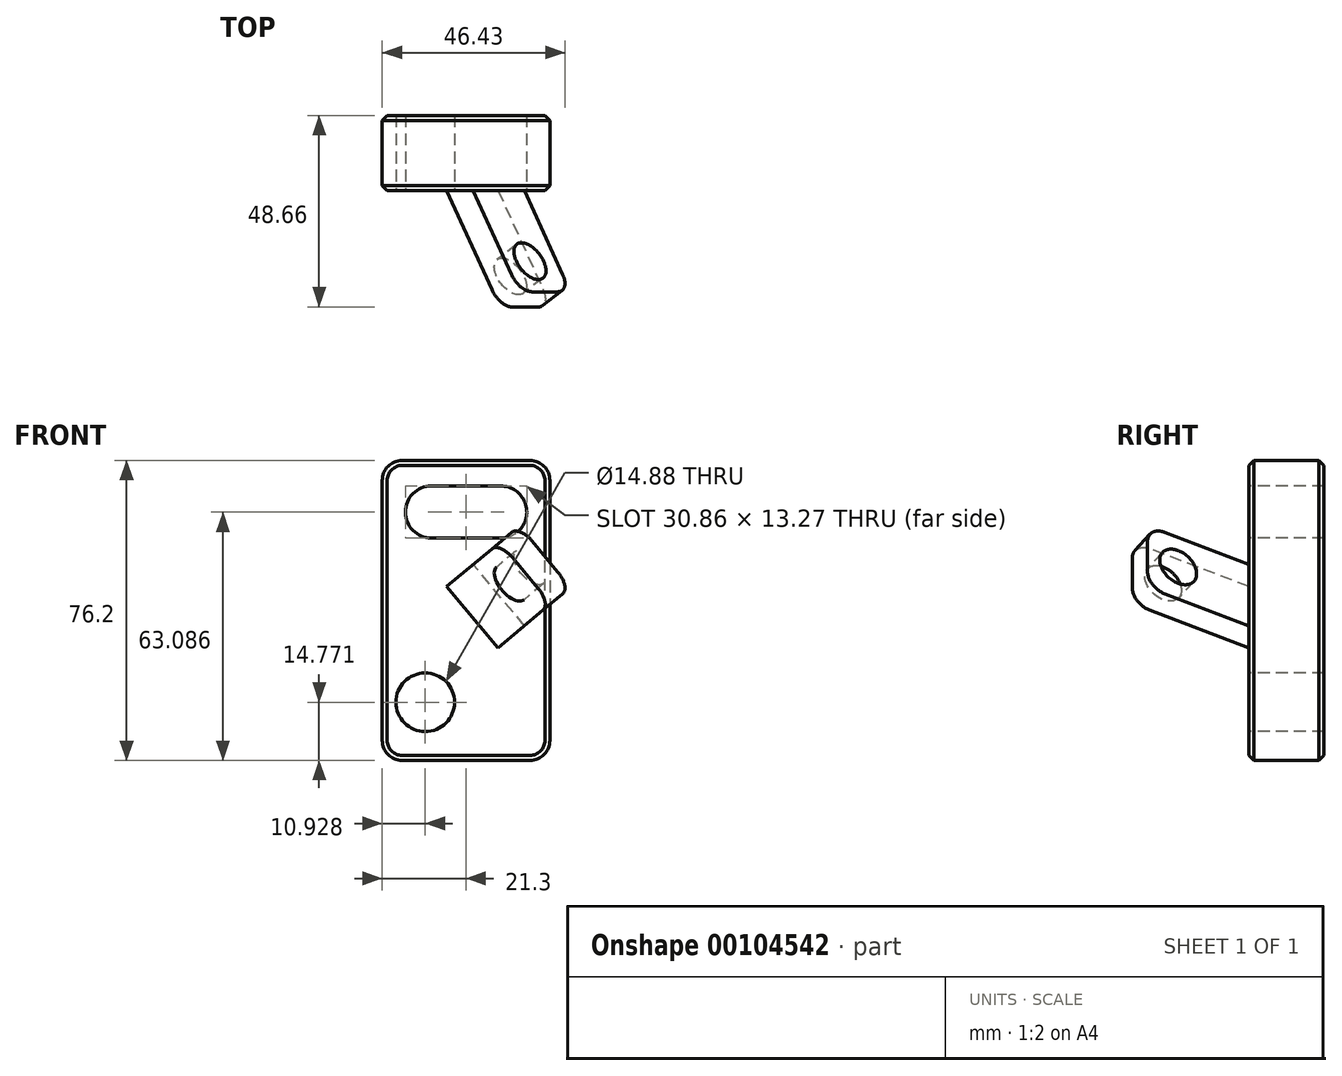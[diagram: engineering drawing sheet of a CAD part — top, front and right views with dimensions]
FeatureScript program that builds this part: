
annotation { "Feature Type Name" : "Feature", "Feature Type Description" : "" }
export const myFeature = defineFeature(function(context is Context, id is Id, definition is map)
    precondition{}
    {
        {
            var Q0;
            Q0=qCreatedBy(makeId("Front.planeOp"),FACE);
            var sketch = newSketch(context, id + "F0", { "sketchPlane" : qUnion([Q0])});
            skLineSegment(sketch, "E0.bottom", {"start": v(21.3, -38.1) * mm, "end": v(-21.3, -38.1) * mm});
            skLineSegment(sketch, "E0.top", {"start": v(21.3, 38.1) * mm, "end": v(-21.3, 38.1) * mm});
            skLineSegment(sketch, "E0.left", {"start": v(21.3, -38.1) * mm, "end": v(21.3, 38.1) * mm});
            skLineSegment(sketch, "E0.right", {"start": v(-21.3, -38.1) * mm, "end": v(-21.3, 38.1) * mm});
            skPoint(sketch, "E0.middle", {"position": v(0, 0) * mm});
            skSolve(sketch);
        }
        {
            var Q0;
            Q0 = qSketchRegion(id + "F0", true);
            extrude(context, id + "F1", {"entities" : qUnion([Q0]), "depth" : 19.05 * mm});
        }
        {
            var Q0;
            Q0=makeQuery(id+"F1.opExtrude","SWEPT_EDGE",EDGE,{"disambiguationData":[OSD([sQuery(id+"F0.wireOp",EDGE,"E0.top"),sQuery(id+"F0.wireOp",EDGE,"E0.right")])]});
            var Q1;
            Q1=makeQuery(id+"F1.opExtrude","SWEPT_EDGE",EDGE,{"disambiguationData":[OSD([sQuery(id+"F0.wireOp",EDGE,"E0.top"),sQuery(id+"F0.wireOp",EDGE,"E0.left")])]});
            var Q2;
            Q2=makeQuery(id+"F1.opExtrude","SWEPT_EDGE",EDGE,{"disambiguationData":[OSD([sQuery(id+"F0.wireOp",EDGE,"E0.bottom"),sQuery(id+"F0.wireOp",EDGE,"E0.left")])]});
            var Q3;
            Q3=makeQuery(id+"F1.opExtrude","SWEPT_EDGE",EDGE,{"disambiguationData":[OSD([sQuery(id+"F0.wireOp",EDGE,"E0.bottom"),sQuery(id+"F0.wireOp",EDGE,"E0.right")])]});
            fillet(context, id + "F2", {"entities" : qUnion([Q0, Q1, Q2, Q3]), "radius" : 5.08 * mm, "tangentPropagation" : true, "allowEdgeOverflow" : false});
        }
        {
            var Q0;
            Q0=makeQuery(id+"F1.opExtrude","CAP_FACE",FACE,{"disambiguationData":[OSD([sQuery(id+"F0.wireOp",EDGE,"E0.bottom"),sQuery(id+"F0.wireOp",EDGE,"E0.top"),sQuery(id+"F0.wireOp",EDGE,"E0.left"),sQuery(id+"F0.wireOp",EDGE,"E0.right")])],"isStart":false});
            var sketch = newSketch(context, id + "F3", { "sketchPlane" : qUnion([Q0])});
            skArc(sketch, "E1", {"start": v(-8.8, 31.62) * mm, "mid": v(-15.43, 24.99) * mm, "end": v(-8.8, 18.35) * mm});
            skArc(sketch, "E2.MirrorC", {"start": v(8.8, 31.62) * mm, "mid": v(15.43, 24.99) * mm, "end": v(8.8, 18.35) * mm});
            skLineSegment(sketch, "E3", {"start": v(-8.8, 31.62) * mm, "end": v(8.8, 31.62) * mm});
            skLineSegment(sketch, "E4", {"start": v(-8.8, 18.35) * mm, "end": v(8.8, 18.35) * mm});
            skCircle(sketch, "E5", {"center": v(-10.37, -23.33) * mm, "radius": 7.44 * mm});
            skSolve(sketch);
        }
        {
            var Q0;
            Q0=makeQuery(id+"F3.imprint","IMPRINT",FACE,{"disambiguationData":[TD([[makeQuery(id+"F3.imprint","IMPRINT",EDGE,{"derivedFrom":sQuery(id+"F3.wireOp",EDGE,"E5")}),1.0]])]});
            var Q1;
            Q1=makeQuery(id+"F3.imprint","IMPRINT",FACE,{"disambiguationData":[TD([[makeQuery(id+"F3.imprint","IMPRINT",EDGE,{"derivedFrom":sQuery(id+"F3.wireOp",EDGE,"E1")}),1.0]])]});
            extrude(context, id + "F4", {"entities" : qUnion([Q0, Q1]), "operationType" : NewBodyOperationType.REMOVE, "oppositeDirection" : true, "depth" : 25.4 * mm});
        }
        {
            var Q0;
            Q0=makeQuery(id+"F1.opExtrude","CAP_FACE",FACE,{"disambiguationData":[OSD([sQuery(id+"F0.wireOp",EDGE,"E0.bottom"),sQuery(id+"F0.wireOp",EDGE,"E0.top"),sQuery(id+"F0.wireOp",EDGE,"E0.left"),sQuery(id+"F0.wireOp",EDGE,"E0.right")])],"isStart":false});
            var sketch = newSketch(context, id + "F5", { "sketchPlane" : qUnion([Q0])});
            skLineSegment(sketch, "E6", {"start": v(-8.08, -9.8) * mm, "end": v(16.46, 10.7) * mm, "construction": true});
            skSolve(sketch);
        }
        {
            var Q0;
            Q0=qCreatedBy(makeId("Top.planeOp"),FACE);
            var Q1;
            Q1=sQuery(id+"F5.wireOp",EDGE,"E6");
            cPlane(context, id + "F6", {"entities" : qUnion([Q0, Q1]), "cplaneType" : CPlaneType.LINE_ANGLE, "offset" : 25.4 * mm, "angle" : 0 * degree, "width" : 152.4 * mm, "height" : 152.4 * mm});
        }
        {
            var Q0;
            Q0=qCreatedBy(id+"F6.planeOp",FACE);
            var sketch = newSketch(context, id + "F7", { "sketchPlane" : qUnion([Q0])});
            skLineSegment(sketch, "E7", {"start": v(8.89, 19.05) * mm, "end": v(0.1, 19.05) * mm});
            skLineSegment(sketch, "E8", {"start": v(0.1, 19.05) * mm, "end": v(17.65, 48.66) * mm});
            skLineSegment(sketch, "E9", {"start": v(17.65, 48.66) * mm, "end": v(24.16, 44.8) * mm});
            skLineSegment(sketch, "E10", {"start": v(24.16, 44.8) * mm, "end": v(8.89, 19.05) * mm});
            skSolve(sketch);
        }
        {
            var Q0;
            Q0 = qSketchRegion(id + "F7", true);
            extrude(context, id + "F8", {"entities" : qUnion([Q0]), "operationType" : NewBodyOperationType.ADD, "endBound" : BoundingType.SYMMETRIC, "depth" : 20.32 * mm});
        }
        {
            var Q0;
            Q0=makeQuery(id+"F8.opExtrude","CAP_EDGE",EDGE,{"disambiguationData":[OSD([sQuery(id+"F7.wireOp",EDGE,"E9")])],"isStart":true});
            var Q1;
            Q1=makeQuery(id+"F8.opExtrude","CAP_EDGE",EDGE,{"disambiguationData":[OSD([sQuery(id+"F7.wireOp",EDGE,"E9")])],"isStart":false});
            fillet(context, id + "F9", {"entities" : qUnion([Q0, Q1]), "radius" : 5.08 * mm, "tangentPropagation" : true, "allowEdgeOverflow" : false});
        }
        {
            var Q0;
            Q0=makeQuery(id+"F8.opExtrude","SWEPT_FACE",FACE,{"disambiguationData":[OSD([sQuery(id+"F7.wireOp",EDGE,"E8")])]});
            var sketch = newSketch(context, id + "F10", { "sketchPlane" : qUnion([Q0])});
            skCircle(sketch, "E11", {"center": v(41.82, -1.93) * mm, "radius": 5.43 * mm});
            skSolve(sketch);
        }
        {
            var Q0;
            Q0 = qSketchRegion(id + "F10", true);
            extrude(context, id + "F11", {"entities" : qUnion([Q0]), "operationType" : NewBodyOperationType.REMOVE, "oppositeDirection" : true, "depth" : 25.4 * mm});
        }
        {
            var Q0;
            Q0=makeQuery(id+"F1.opExtrude","CAP_EDGE",EDGE,{"disambiguationData":[OSD([sQuery(id+"F0.wireOp",EDGE,"E0.right")])],"isStart":false});
            var Q1;
            Q1=makeQuery(id+"F1.opExtrude","CAP_EDGE",EDGE,{"disambiguationData":[OSD([sQuery(id+"F0.wireOp",EDGE,"E0.right")])],"isStart":true});
            chamfer(context, id + "F12", {"entities" : qUnion([Q0, Q1]), "width" : 1.27 * mm, "tangentPropagation" : true});
        }
    });
